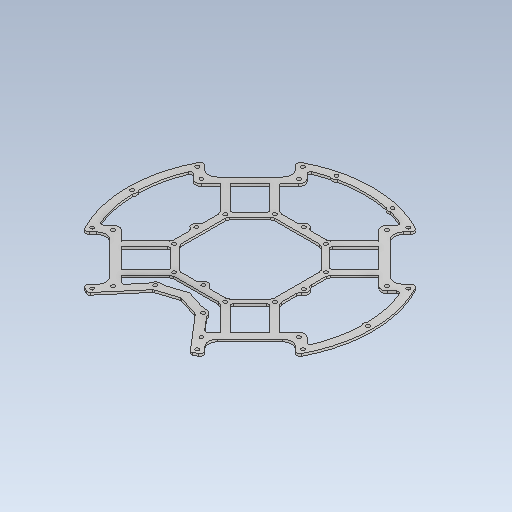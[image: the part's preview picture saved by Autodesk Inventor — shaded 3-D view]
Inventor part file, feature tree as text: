
AUTODESK INVENTOR PART (.ipt)
format: ipt  version: 2020 (Build 240168000, 168)  size: 917,504 bytes
history: native  units: mm
features: extrude x8, sketch x5, projected_geometry x4, other x1
ambient origin geometry x8: Origin, YZ Plane, XZ Plane, XY Plane, X Axis, Y Axis, Z Axis, Center Point
bodies: Body1 (feature_tree)
feature tree (18):
  other  "Твердое тело1"
  extrude  "outer"  TaperAngle=45.0deg  [1 undecoded]
  extrude  "inner"  Depth=7.0mm
  sketch  "Эскиз3"
  extrude  "Выдавливание3"  Depth=20.0mm
  extrude  "Выдавливание4"  Depth=7.0mm
  sketch  "Эскиз4"
  extrude  "Выдавливание5"  Depth=3.2mm
  extrude  "Выдавливание6"  Depth=59.0mm
  sketch  "Эскиз5"
  extrude  "Выдавливание7"  Depth=83.0mm
  extrude  "Выдавливание8"  Depth=69.0mm
  sketch  "Эскиз1"
  sketch  "Эскиз2"
  projected_geometry  "Спроецированная петля1"
  projected_geometry  "Спроецированная петля2"
  projected_geometry  "Спроецированная петля3"
  projected_geometry  "Спроецированная петля4"
note: 1 required parameter value undecoded (feature->parameter linkage not recoverable at this tier; creation-order binding heuristic only, values carry confidence <= 0.55)
